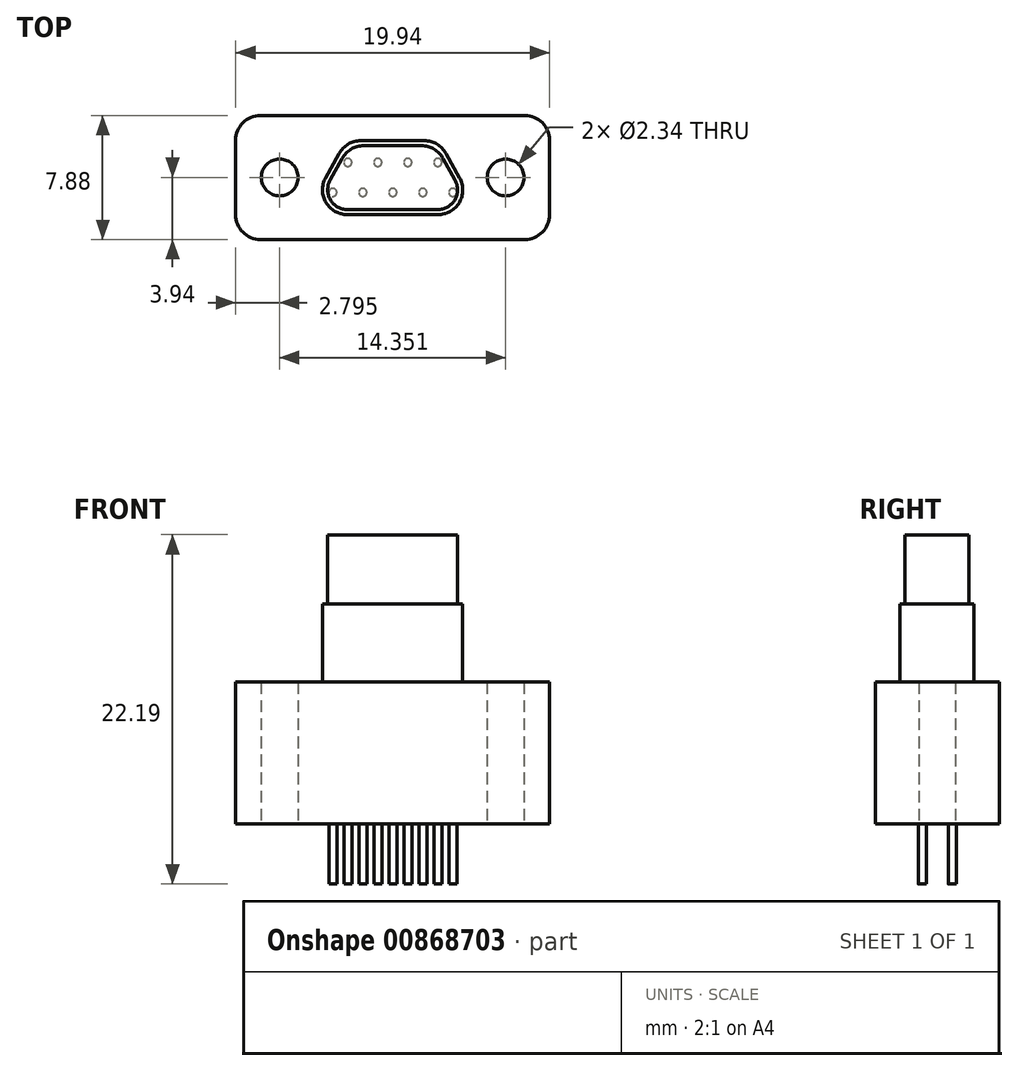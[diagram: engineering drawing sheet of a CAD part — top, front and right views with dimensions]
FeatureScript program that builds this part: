
annotation { "Feature Type Name" : "Feature", "Feature Type Description" : "" }
export const myFeature = defineFeature(function(context is Context, id is Id, definition is map)
    precondition{}
    {
        {
            var Q0;
            Q0=qCreatedBy(makeId("Top.planeOp"),FACE);
            var sketch = newSketch(context, id + "F0", { "sketchPlane" : qUnion([Q0])});
            skLineSegment(sketch, "E0.bottom", {"start": v(-8.4, 3.94) * mm, "end": v(8.4, 3.94) * mm});
            skLineSegment(sketch, "E0.top", {"start": v(-8.4, -3.94) * mm, "end": v(8.4, -3.94) * mm});
            skLineSegment(sketch, "E0.left", {"start": v(-9.97, 2.36) * mm, "end": v(-9.97, -2.36) * mm});
            skLineSegment(sketch, "E0.right", {"start": v(9.97, 2.36) * mm, "end": v(9.97, -2.36) * mm});
            skPoint(sketch, "E0.middle", {"position": v(0, 0) * mm});
            skCircle(sketch, "E1", {"center": v(-7.18, 0) * mm, "radius": 1.17 * mm});
            skCircle(sketch, "E2", {"center": v(7.18, 0) * mm, "radius": 1.17 * mm});
            skPoint(sketch, "E3.visualSharp", {"position": v(-9.97, -3.94) * mm});
            skArc(sketch, "E3.filletArc", {"start": v(-9.97, -2.36) * mm, "mid": v(-9.5, -3.48) * mm, "end": v(-8.4, -3.94) * mm});
            skPoint(sketch, "E4.visualSharp", {"position": v(-9.97, 3.94) * mm});
            skArc(sketch, "E4.filletArc", {"start": v(-8.4, 3.94) * mm, "mid": v(-9.5, 3.48) * mm, "end": v(-9.97, 2.36) * mm});
            skPoint(sketch, "E5.visualSharp", {"position": v(9.97, 3.94) * mm});
            skArc(sketch, "E5.filletArc", {"start": v(9.97, 2.36) * mm, "mid": v(9.5, 3.48) * mm, "end": v(8.4, 3.94) * mm});
            skPoint(sketch, "E6.visualSharp", {"position": v(9.97, -3.94) * mm});
            skArc(sketch, "E6.filletArc", {"start": v(8.4, -3.94) * mm, "mid": v(9.5, -3.48) * mm, "end": v(9.97, -2.36) * mm});
            skSolve(sketch);
        }
        {
            var Q0;
            Q0=makeQuery(id+"F0.imprint","IMPRINT",FACE,{"disambiguationData":[TD([[makeQuery(id+"F0.imprint","IMPRINT",EDGE,{"derivedFrom":sQuery(id+"F0.wireOp",EDGE,"E0.bottom")}),-1.0]])]});
            extrude(context, id + "F1", {"entities" : qUnion([Q0]), "endBound" : BoundingType.SYMMETRIC, "depth" : 9.02 * mm, "offsetDistance" : 25.4 * mm});
        }
        {
            var Q0;
            Q0=makeQuery(id+"F1.opExtrude","CAP_FACE",FACE,{"disambiguationData":[OSD([sQuery(id+"F0.wireOp",EDGE,"E0.bottom"),sQuery(id+"F0.wireOp",EDGE,"E0.top"),sQuery(id+"F0.wireOp",EDGE,"E0.left"),sQuery(id+"F0.wireOp",EDGE,"E0.right"),sQuery(id+"F0.wireOp",EDGE,"E1"),sQuery(id+"F0.wireOp",EDGE,"E2"),sQuery(id+"F0.wireOp",EDGE,"E3.filletArc"),sQuery(id+"F0.wireOp",EDGE,"E4.filletArc"),sQuery(id+"F0.wireOp",EDGE,"E5.filletArc"),sQuery(id+"F0.wireOp",EDGE,"E6.filletArc")])],"isStart":false});
            var sketch = newSketch(context, id + "F2", { "sketchPlane" : qUnion([Q0])});
            skPoint(sketch, "E7.middle", {"position": v(0, 0) * mm});
            skLineSegment(sketch, "E8.top", {"start": v(2.88, -2.36) * mm, "end": v(-2.88, -2.36) * mm});
            skLineSegment(sketch, "E9", {"start": v(-2.02, 2.34) * mm, "end": v(2.02, 2.34) * mm});
            skLineSegment(sketch, "E10", {"start": v(-4.25, -0.02) * mm, "end": v(-3.4, 1.53) * mm});
            skLineSegment(sketch, "E11", {"start": v(3.4, 1.53) * mm, "end": v(4.26, -0.02) * mm});
            skPoint(sketch, "E12.visualSharp", {"position": v(-2.95, 2.34) * mm});
            skArc(sketch, "E12.filletArc", {"start": v(-2.02, 2.34) * mm, "mid": v(-2.82, 2.12) * mm, "end": v(-3.4, 1.53) * mm});
            skPoint(sketch, "E13.visualSharp", {"position": v(-5.55, -2.36) * mm});
            skArc(sketch, "E13.filletArc", {"start": v(-4.25, -0.02) * mm, "mid": v(-4.23, -1.59) * mm, "end": v(-2.88, -2.36) * mm});
            skPoint(sketch, "E14.visualSharp", {"position": v(5.55, -2.36) * mm});
            skArc(sketch, "E14.filletArc", {"start": v(2.88, -2.36) * mm, "mid": v(4.23, -1.59) * mm, "end": v(4.26, -0.02) * mm});
            skPoint(sketch, "E15.visualSharp", {"position": v(2.95, 2.34) * mm});
            skArc(sketch, "E15.filletArc", {"start": v(3.4, 1.53) * mm, "mid": v(2.82, 2.12) * mm, "end": v(2.02, 2.34) * mm});
            skSolve(sketch);
        }
        {
            var Q0;
            Q0=qSketchRegion(id+"F2",true);
            extrude(context, id + "F3", {"entities" : qUnion([Q0]), "operationType" : NewBodyOperationType.ADD, "depth" : 4.95 * mm, "offsetDistance" : 25.4 * mm});
        }
        {
            var Q0;
            Q0=makeQuery(id+"F3.opExtrude","CAP_FACE",FACE,{"disambiguationData":[OSD([sQuery(id+"F2.wireOp",EDGE,"E8.top"),sQuery(id+"F2.wireOp",EDGE,"E9"),sQuery(id+"F2.wireOp",EDGE,"E10"),sQuery(id+"F2.wireOp",EDGE,"E11"),sQuery(id+"F2.wireOp",EDGE,"E12.filletArc"),sQuery(id+"F2.wireOp",EDGE,"E13.filletArc"),sQuery(id+"F2.wireOp",EDGE,"E14.filletArc"),sQuery(id+"F2.wireOp",EDGE,"E15.filletArc")])],"isStart":false});
            var sketch = newSketch(context, id + "F4", { "sketchPlane" : qUnion([Q0])});
            skLineSegment(sketch, "E16", {"start": v(-1.83, 2.02) * mm, "end": v(1.83, 2.02) * mm});
            skLineSegment(sketch, "E17", {"start": v(3.2, 1.2) * mm, "end": v(3.97, -0.16) * mm});
            skLineSegment(sketch, "E18", {"start": v(2.86, -2.04) * mm, "end": v(-2.85, -2.04) * mm});
            skLineSegment(sketch, "E19", {"start": v(-3.97, -0.16) * mm, "end": v(-3.2, 1.2) * mm});
            skPoint(sketch, "E20.visualSharp", {"position": v(-5.01, -2.04) * mm});
            skArc(sketch, "E20.filletArc", {"start": v(-3.97, -0.16) * mm, "mid": v(-3.95, -1.42) * mm, "end": v(-2.85, -2.04) * mm});
            skPoint(sketch, "E21.visualSharp", {"position": v(-2.76, 2.02) * mm});
            skArc(sketch, "E21.filletArc", {"start": v(-1.83, 2.02) * mm, "mid": v(-2.63, 1.8) * mm, "end": v(-3.2, 1.2) * mm});
            skPoint(sketch, "E22.visualSharp", {"position": v(2.76, 2.02) * mm});
            skArc(sketch, "E22.filletArc", {"start": v(3.2, 1.2) * mm, "mid": v(2.63, 1.8) * mm, "end": v(1.83, 2.02) * mm});
            skPoint(sketch, "E23.visualSharp", {"position": v(5.01, -2.04) * mm});
            skArc(sketch, "E23.filletArc", {"start": v(2.86, -2.04) * mm, "mid": v(3.95, -1.42) * mm, "end": v(3.97, -0.16) * mm});
            skSolve(sketch);
        }
        {
            var Q0;
            Q0=qSketchRegion(id+"F4",true);
            extrude(context, id + "F5", {"entities" : qUnion([Q0]), "operationType" : NewBodyOperationType.ADD, "depth" : 4.4 * mm, "offsetDistance" : 25.4 * mm});
        }
        {
            var Q0;
            Q0=makeQuery(id+"F1.opExtrude","CAP_FACE",FACE,{"disambiguationData":[OSD([sQuery(id+"F0.wireOp",EDGE,"E0.bottom"),sQuery(id+"F0.wireOp",EDGE,"E0.top"),sQuery(id+"F0.wireOp",EDGE,"E0.left"),sQuery(id+"F0.wireOp",EDGE,"E0.right"),sQuery(id+"F0.wireOp",EDGE,"E1"),sQuery(id+"F0.wireOp",EDGE,"E2"),sQuery(id+"F0.wireOp",EDGE,"E3.filletArc"),sQuery(id+"F0.wireOp",EDGE,"E4.filletArc"),sQuery(id+"F0.wireOp",EDGE,"E5.filletArc"),sQuery(id+"F0.wireOp",EDGE,"E6.filletArc")])],"isStart":true});
            var sketch = newSketch(context, id + "F6", { "sketchPlane" : qUnion([Q0])});
            skCircle(sketch, "E24", {"center": v(-3.8, 0.95) * mm, "radius": 0.25 * mm});
            skCircle(sketch, "E25.1.0.0", {"center": v(-1.9, 0.95) * mm, "radius": 0.25 * mm});
            skCircle(sketch, "E25.2.0.0", {"center": v(0.01, 0.95) * mm, "radius": 0.25 * mm});
            skCircle(sketch, "E25.3.0.0", {"center": v(1.92, 0.95) * mm, "radius": 0.25 * mm});
            skCircle(sketch, "E25.4.0.0", {"center": v(3.82, 0.95) * mm, "radius": 0.25 * mm});
            skLineSegment(sketch, "E25.direction1", {"start": v(-3.8, 0.95) * mm, "end": v(-1.9, 0.95) * mm, "construction": true});
            skCircle(sketch, "E26", {"center": v(-2.84, -0.95) * mm, "radius": 0.25 * mm});
            skCircle(sketch, "E27.1.0.0", {"center": v(-0.94, -0.95) * mm, "radius": 0.25 * mm});
            skCircle(sketch, "E27.2.0.0", {"center": v(0.97, -0.95) * mm, "radius": 0.25 * mm});
            skCircle(sketch, "E27.3.0.0", {"center": v(2.87, -0.95) * mm, "radius": 0.25 * mm});
            skLineSegment(sketch, "E27.direction1", {"start": v(-2.84, -0.95) * mm, "end": v(-0.94, -0.95) * mm, "construction": true});
            skSolve(sketch);
        }
        {
            var Q0;
            Q0=qSketchRegion(id+"F6",true);
            extrude(context, id + "F7", {"entities" : qUnion([Q0]), "operationType" : NewBodyOperationType.ADD, "depth" : 3.8 * mm, "offsetDistance" : 25.4 * mm});
        }
    });
